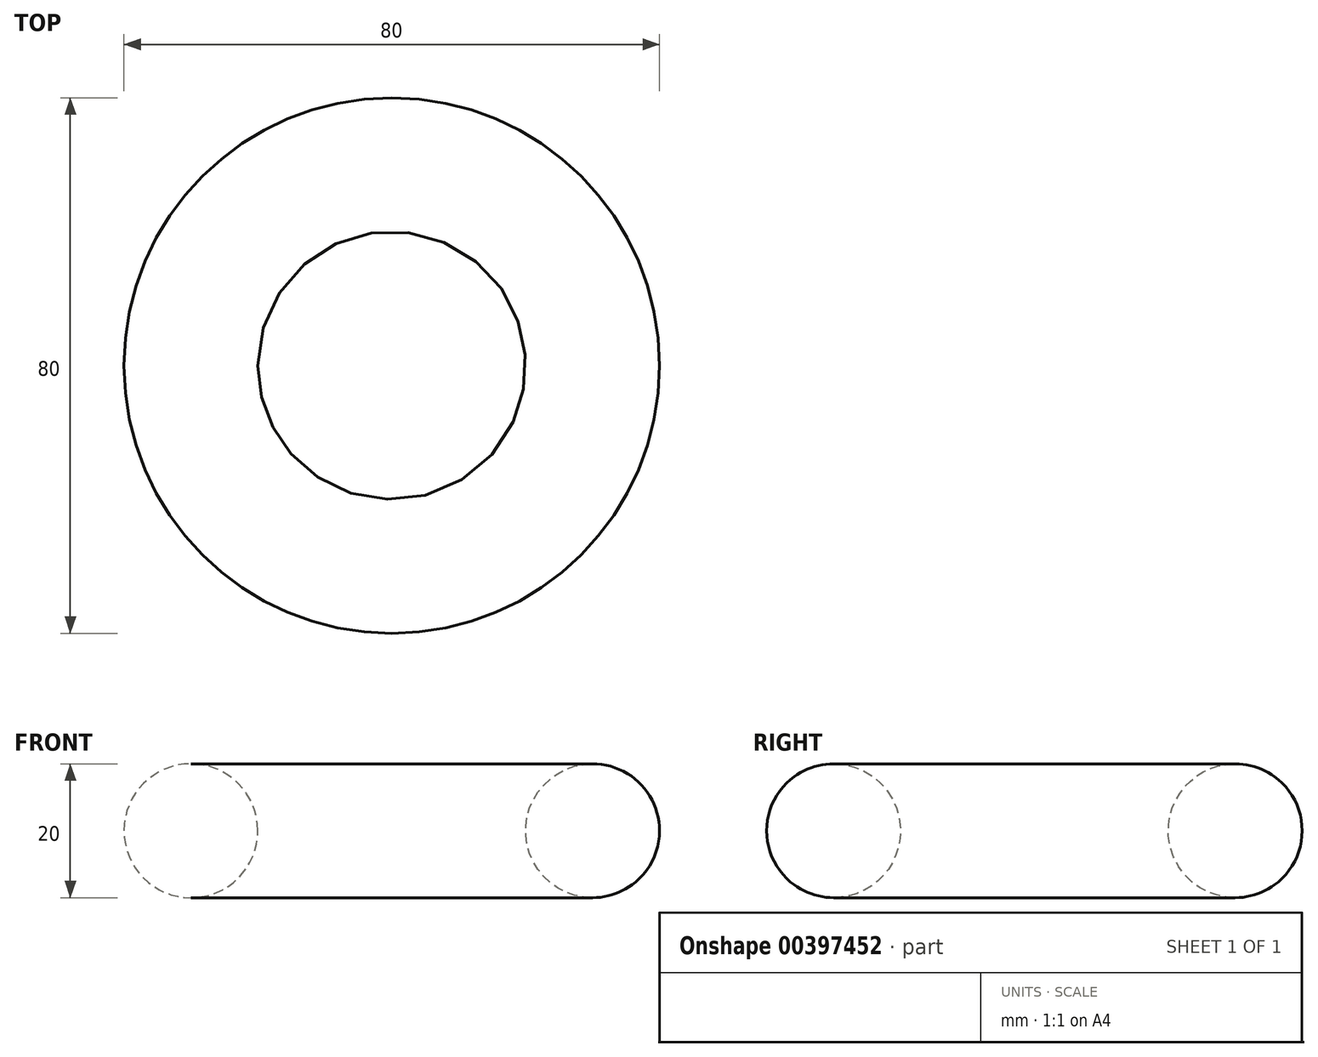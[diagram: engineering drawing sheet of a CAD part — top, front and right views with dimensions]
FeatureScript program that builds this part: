
annotation { "Feature Type Name" : "Feature", "Feature Type Description" : "" }
export const myFeature = defineFeature(function(context is Context, id is Id, definition is map)
    precondition{}
    {
        {
            var Q0;
            Q0=qCreatedBy(makeId("Top.planeOp"),FACE);
            var sketch = newSketch(context, id + "F0", { "sketchPlane" : qUnion([Q0])});
            skCircle(sketch, "E0", {"center": v(0, 0) * mm, "radius": 40 * mm});
            skSolve(sketch);
        }
        {
            var Q0;
            Q0=qCreatedBy(makeId("Front.planeOp"),FACE);
            var sketch = newSketch(context, id + "F1", { "sketchPlane" : qUnion([Q0])});
            skCircle(sketch, "E1", {"center": v(-30, 0) * mm, "radius": 10 * mm});
            skSolve(sketch);
        }
        {
            var Q0;
            Q0=makeQuery(id+"F1.imprint","IMPRINT",FACE,{"disambiguationData":[TD([[makeQuery(id+"F1.imprint","IMPRINT",EDGE,{"derivedFrom":sQuery(id+"F1.wireOp",EDGE,"E1")}),1.0]])]});
            var Q1;
            Q1=sQuery(id+"F0.wireOp",EDGE,"E0");
            revolve(context, id + "F2", {"surfaceOperationType" : NewSurfaceOperationType.NEW, "entities" : qUnion([Q0]), "axis" : qUnion([Q1]), "revolveType" : RevolveType.FULL});
        }
    });
